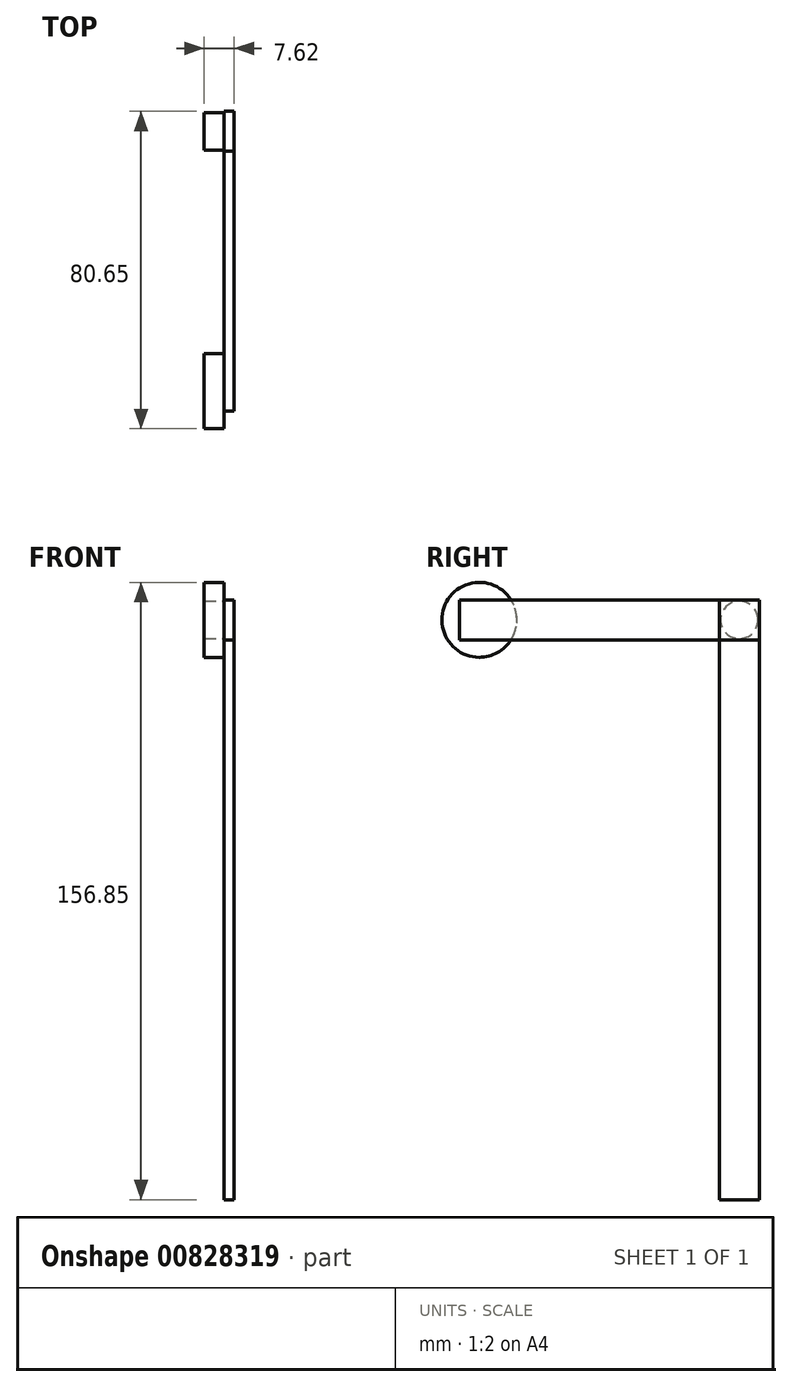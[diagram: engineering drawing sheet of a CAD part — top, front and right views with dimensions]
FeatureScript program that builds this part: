
annotation { "Feature Type Name" : "Feature", "Feature Type Description" : "" }
export const myFeature = defineFeature(function(context is Context, id is Id, definition is map)
    precondition{}
    {
        {
            var Q0;
            Q0=qCreatedBy(makeId("Right.planeOp"),FACE);
            var sketch = newSketch(context, id + "F0", { "sketchPlane" : qUnion([Q0])});
            skLineSegment(sketch, "E0.bottom", {"start": v(-5.08, 5.08) * mm, "end": v(71.12, 5.08) * mm});
            skLineSegment(sketch, "E0.top", {"start": v(-5.08, -5.08) * mm, "end": v(71.12, -5.08) * mm});
            skLineSegment(sketch, "E0.left", {"start": v(-5.08, 5.08) * mm, "end": v(-5.08, -5.08) * mm});
            skLineSegment(sketch, "E0.right", {"start": v(71.12, 5.08) * mm, "end": v(71.12, -5.08) * mm});
            skSolve(sketch);
        }
        {
            var Q0;
            Q0 = qSketchRegion(id + "F0", true);
            extrude(context, id + "F1", {"entities" : qUnion([Q0]), "depth" : 2.54 * mm, "offsetDistance" : 25.4 * mm});
        }
        {
            var Q0;
            Q0=qCreatedBy(makeId("Right.planeOp"),FACE);
            var sketch = newSketch(context, id + "F2", { "sketchPlane" : qUnion([Q0])});
            skCircle(sketch, "E1", {"center": v(0, 0) * mm, "radius": 9.53 * mm});
            skCircle(sketch, "E2", {"center": v(66.04, 0) * mm, "radius": 4.76 * mm});
            skSolve(sketch);
        }
        {
            var Q0;
            Q0 = qSketchRegion(id + "F2", true);
            extrude(context, id + "F3", {"entities" : qUnion([Q0]), "oppositeDirection" : true, "depth" : 5.08 * mm, "offsetDistance" : 25.4 * mm});
        }
        {
            var Q0;
            Q0=qCreatedBy(makeId("Right.planeOp"),FACE);
            var sketch = newSketch(context, id + "F4", { "sketchPlane" : qUnion([Q0])});
            skLineSegment(sketch, "E3.bottom", {"start": v(60.96, 5.08) * mm, "end": v(71.12, 5.08) * mm});
            skLineSegment(sketch, "E3.top", {"start": v(60.96, -147.32) * mm, "end": v(71.12, -147.32) * mm});
            skLineSegment(sketch, "E3.left", {"start": v(60.96, 5.08) * mm, "end": v(60.96, -147.32) * mm});
            skLineSegment(sketch, "E3.right", {"start": v(71.12, 5.08) * mm, "end": v(71.12, -147.32) * mm});
            skSolve(sketch);
        }
        {
            var Q0;
            Q0 = qSketchRegion(id + "F4", true);
            extrude(context, id + "F5", {"entities" : qUnion([Q0]), "depth" : 2.54 * mm, "offsetDistance" : 25.4 * mm});
        }
    });
